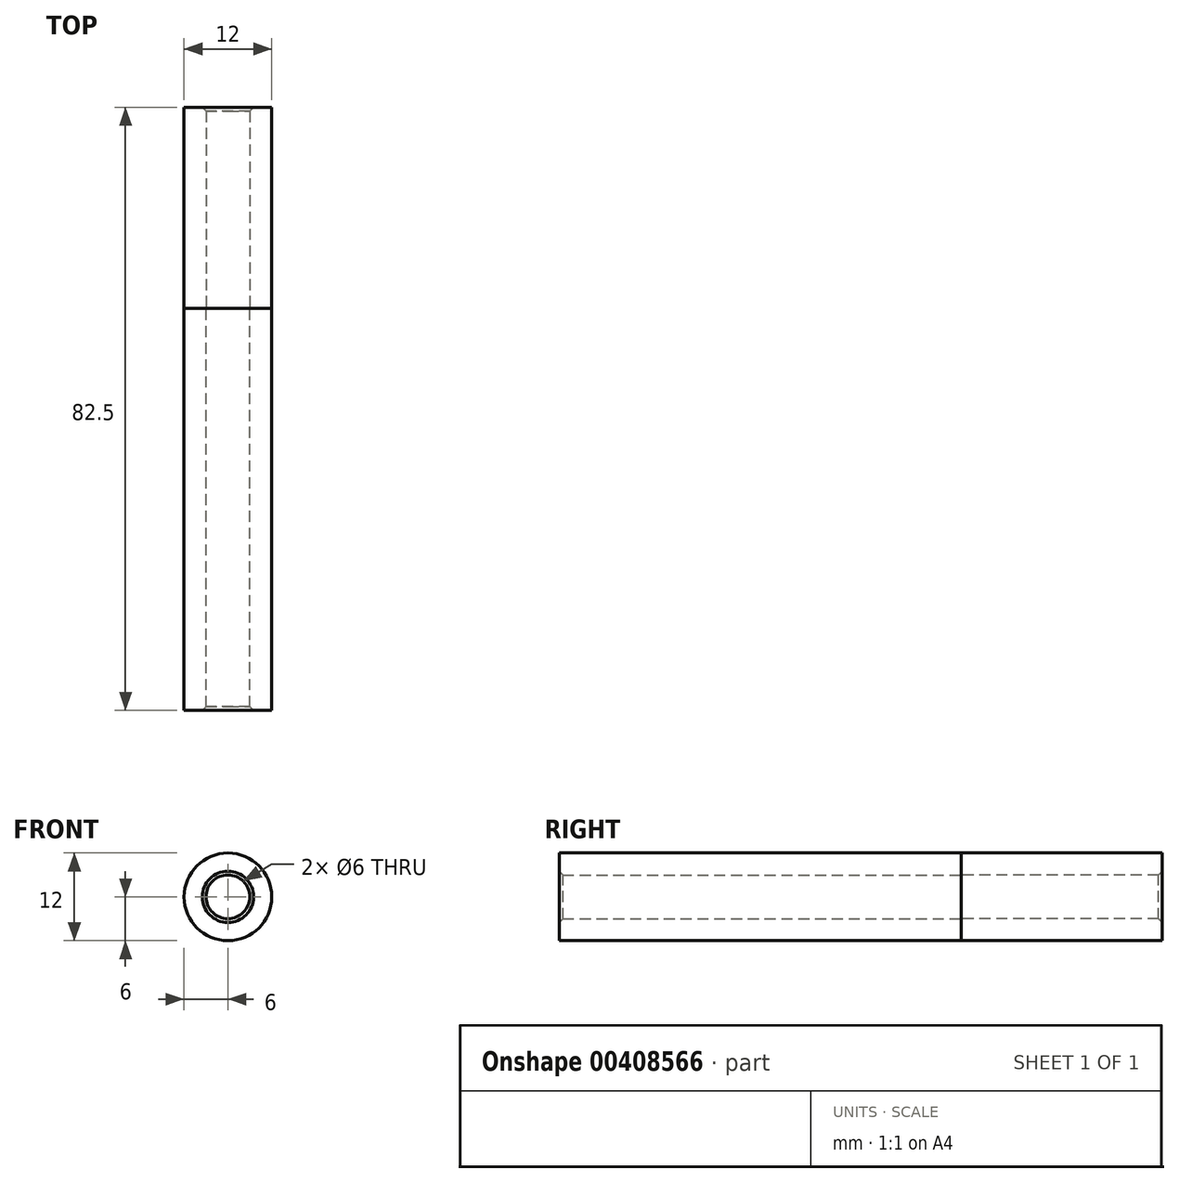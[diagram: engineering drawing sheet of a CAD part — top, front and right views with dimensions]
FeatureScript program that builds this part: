
annotation { "Feature Type Name" : "Feature", "Feature Type Description" : "" }
export const myFeature = defineFeature(function(context is Context, id is Id, definition is map)
    precondition{}
    {
        {
            var Q0;
            Q0=qCreatedBy(makeId("Front.planeOp"),FACE);
            var sketch = newSketch(context, id + "F0", { "sketchPlane" : qUnion([Q0])});
            skPoint(sketch, "E0.middle", {"position": v(0, 0) * mm});
            skCircle(sketch, "E1", {"center": v(0, 0) * mm, "radius": 6 * mm});
            skCircle(sketch, "E2", {"center": v(0, 0) * mm, "radius": 3 * mm});
            skSolve(sketch);
        }
        {
            var Q0;
            Q0=makeQuery(id+"F0.imprint","IMPRINT",FACE,{"disambiguationData":[TD([[makeQuery(id+"F0.imprint","IMPRINT",EDGE,{"derivedFrom":sQuery(id+"F0.wireOp",EDGE,"E1")}),1.0]])]});
            extrude(context, id + "F1", {"entities" : qUnion([Q0]), "depth" : 55 * mm});
        }
        {
            var Q0;
            Q0=makeQuery(id+"F1.opExtrude","CAP_EDGE",EDGE,{"disambiguationData":[OSD([sQuery(id+"F0.wireOp",EDGE,"E2")])],"isStart":false});
            chamfer(context, id + "F2", {"entities" : qUnion([Q0]), "width" : 0.5 * mm, "tangentPropagation" : true});
        }
        {
            var Q0;
            Q0=makeQuery(id+"F0.imprint","IMPRINT",FACE,{"disambiguationData":[TD([[makeQuery(id+"F0.imprint","IMPRINT",EDGE,{"derivedFrom":sQuery(id+"F0.wireOp",EDGE,"E1")}),1.0]])]});
            extrude(context, id + "F3", {"entities" : qUnion([Q0]), "oppositeDirection" : true, "depth" : 27.5 * mm});
        }
        {
            var Q0;
            Q0=makeQuery(id+"F3.opExtrude","CAP_EDGE",EDGE,{"disambiguationData":[OSD([sQuery(id+"F0.wireOp",EDGE,"E2")])],"isStart":false});
            chamfer(context, id + "F4", {"entities" : qUnion([Q0]), "width" : 0.5 * mm, "tangentPropagation" : true});
        }
    });
